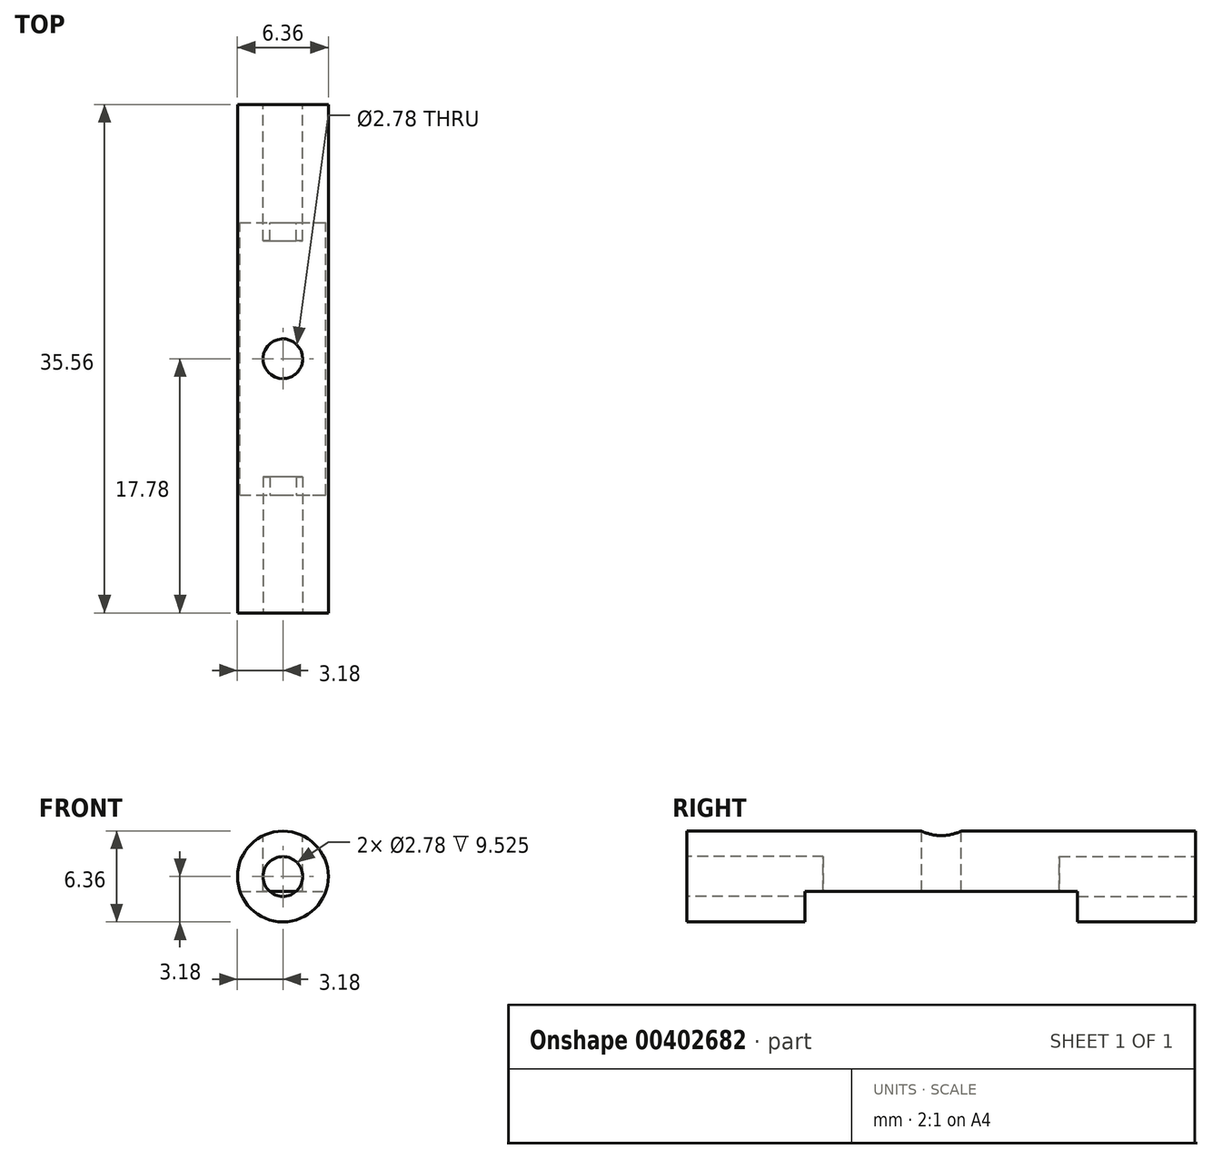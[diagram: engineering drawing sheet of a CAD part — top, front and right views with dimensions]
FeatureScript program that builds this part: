
annotation { "Feature Type Name" : "Feature", "Feature Type Description" : "" }
export const myFeature = defineFeature(function(context is Context, id is Id, definition is map)
    precondition{}
    {
        {
            var Q0;
            Q0=qCreatedBy(makeId("Front.planeOp"),FACE);
            var sketch = newSketch(context, id + "F0", { "sketchPlane" : qUnion([Q0])});
            skCircle(sketch, "E0", {"center": v(0, 0) * mm, "radius": 3.18 * mm});
            skSolve(sketch);
        }
        {
            var Q0;
            Q0 = qSketchRegion(id + "F0", true);
            extrude(context, id + "F1", {"entities" : qUnion([Q0]), "endBound" : BoundingType.SYMMETRIC, "depth" : 35.56 * mm});
        }
        {
            var Q0;
            Q0=makeQuery(id+"F1.opExtrude","CAP_FACE",FACE,{"disambiguationData":[OSD([sQuery(id+"F0.wireOp",EDGE,"E0")])],"isStart":false});
            var sketch = newSketch(context, id + "F2", { "sketchPlane" : qUnion([Q0])});
            skCircle(sketch, "E1", {"center": v(0, 0) * mm, "radius": 1.39 * mm});
            skSolve(sketch);
        }
        {
            var Q0;
            Q0 = qSketchRegion(id + "F2", true);
            extrude(context, id + "F3", {"entities" : qUnion([Q0]), "operationType" : NewBodyOperationType.REMOVE, "oppositeDirection" : true, "depth" : 9.52 * mm});
        }
        {
            var Q0;
            Q0=makeQuery(id+"F1.opExtrude","CAP_FACE",FACE,{"disambiguationData":[OSD([sQuery(id+"F0.wireOp",EDGE,"E0")])],"isStart":true});
            var sketch = newSketch(context, id + "F4", { "sketchPlane" : qUnion([Q0])});
            skCircle(sketch, "E2", {"center": v(0, 0) * mm, "radius": 1.39 * mm});
            skSolve(sketch);
        }
        {
            var Q0;
            Q0 = qSketchRegion(id + "F4", true);
            extrude(context, id + "F5", {"entities" : qUnion([Q0]), "operationType" : NewBodyOperationType.REMOVE, "oppositeDirection" : true, "depth" : 9.52 * mm});
        }
        {
            var Q0;
            Q0=qCreatedBy(makeId("Front.planeOp"),FACE);
            var sketch = newSketch(context, id + "F6", { "sketchPlane" : qUnion([Q0])});
            skLineSegment(sketch, "E3.bottom", {"start": v(-9.88, -3.2) * mm, "end": v(9.17, -3.2) * mm});
            skLineSegment(sketch, "E3.top", {"start": v(-9.88, -1.04) * mm, "end": v(9.17, -1.04) * mm});
            skLineSegment(sketch, "E3.left", {"start": v(-9.88, -3.2) * mm, "end": v(-9.88, -1.04) * mm});
            skLineSegment(sketch, "E3.right", {"start": v(9.17, -3.2) * mm, "end": v(9.17, -1.04) * mm});
            skSolve(sketch);
        }
        {
            var Q0;
            Q0 = qSketchRegion(id + "F6", true);
            extrude(context, id + "F7", {"entities" : qUnion([Q0]), "operationType" : NewBodyOperationType.REMOVE, "endBound" : BoundingType.SYMMETRIC, "depth" : 19.05 * mm});
        }
        {
            var Q0;
            Q0=qCreatedBy(makeId("Top.planeOp"),FACE);
            var sketch = newSketch(context, id + "F8", { "sketchPlane" : qUnion([Q0])});
            skCircle(sketch, "E4", {"center": v(0, 0) * mm, "radius": 1.39 * mm});
            skSolve(sketch);
        }
        {
            var Q0;
            Q0 = qSketchRegion(id + "F8", true);
            extrude(context, id + "F9", {"entities" : qUnion([Q0]), "operationType" : NewBodyOperationType.REMOVE, "endBound" : BoundingType.SYMMETRIC, "oppositeDirection" : true, "depth" : 6.35 * mm});
        }
    });
